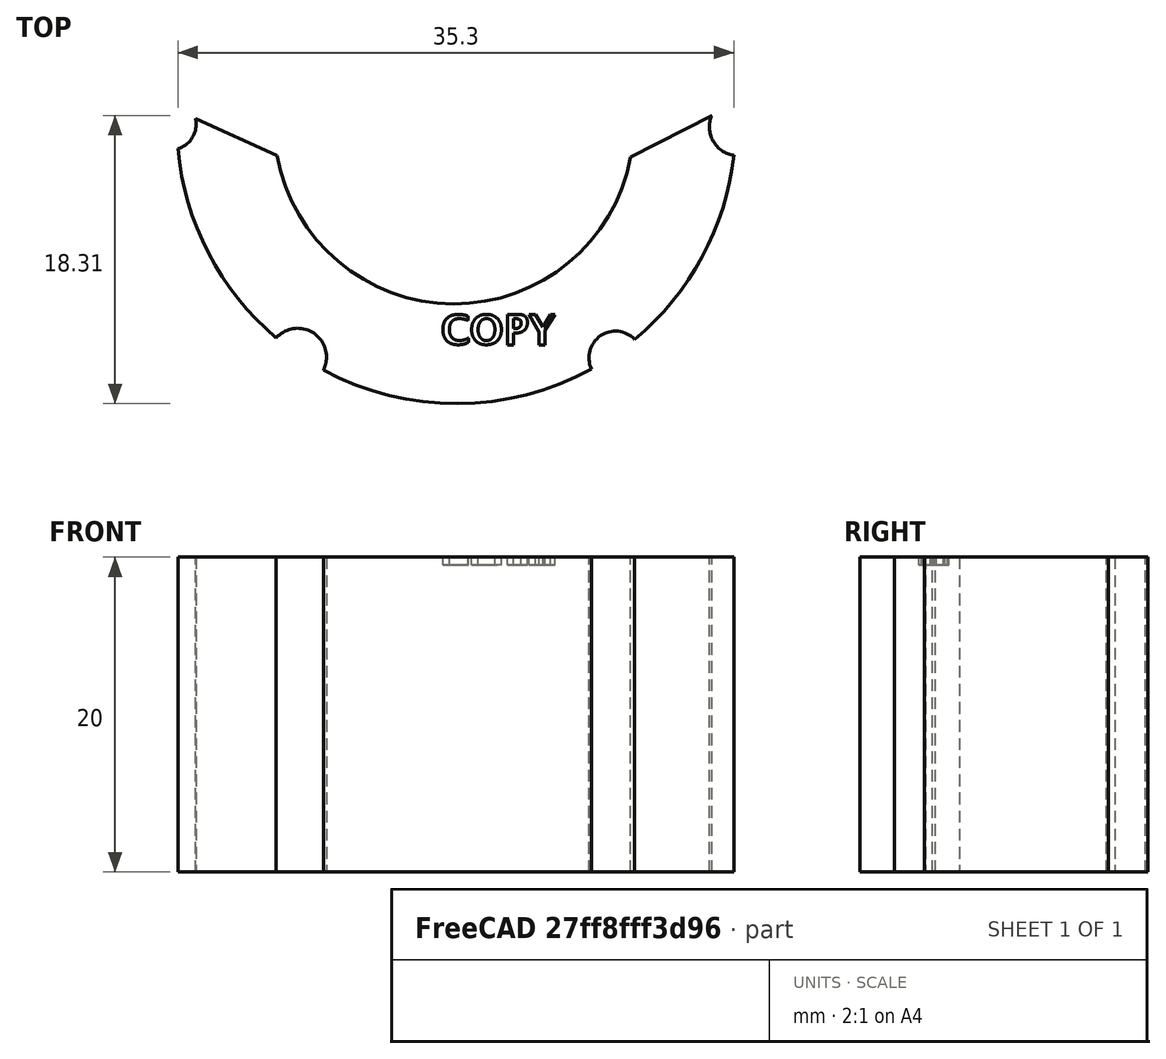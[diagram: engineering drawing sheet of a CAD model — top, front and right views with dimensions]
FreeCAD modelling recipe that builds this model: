
FCSTD DOCUMENT  (FreeCAD 0.18R4 (GitTag))
Label: Pad -copy
License: All rights reserved
LicenseURL: http://en.wikipedia.org/wiki/All_rights_reserved
objects: Sketcher::SketchObject×3, PartDesign::Pocket×2, PartDesign::Pad×1, PartDesign::Body×1, Part::Part2DObjectPython×1, Part::Extrusion×1, Part::Cut×1
note: 13 computed .brp shape members not serialized (recipe doc carries the construction recipe); baked Part::Feature solids carry a one-line shape summary decoded from their .brp

FEATURE [Sketcher::SketchObject] Sketch044
  MapMode = 5
  Support = -> [XY_Plane010]
  sketch-geometry (4):
    g0: ArcOfCircle CenterX=-0.026819 CenterY=0.000339 CenterZ=0 NormalX=0 NormalY=0 NormalZ=1 AngleXU=0 Radius=17.7391 StartAngle=3.09077 EndAngle=6.35772
    g1: ArcOfCircle CenterX=-0.16597 CenterY=0.00513446 CenterZ=0 NormalX=0 NormalY=0 NormalZ=1 AngleXU=0 Radius=11.4055 StartAngle=3.31589 EndAngle=6.09959
    g2: LineSegment StartX=-11.3987 StartY=-1.97276 StartZ=0 EndX=-17.743 EndY=0.901444 EndZ=0
    g3: LineSegment StartX=17.663 StartY=1.32135 StartZ=0 EndX=11.0479 EndY=-2.07709 EndZ=0
  constraints (4):
    c: Coincident(g2,g1)
    c: Coincident(g2,g0)
    c: Coincident(g3,g0)
    c: Coincident(g3,g1)
FEATURE [PartDesign::Pad] Pad013  label="Main body"
  Length = 20
  Length2 = 100
  Profile = -> Sketch044
  Type = 0
FEATURE [Sketcher::SketchObject] Sketch043
  MapMode = 5
  Placement = pos=(0,0,20) rot=(0,0,1;0rad)
  Support = -> [Pad013]
  sketch-geometry (2):
    g0: Circle CenterX=-18.1521 CenterY=0 CenterZ=0 NormalX=0 NormalY=0 NormalZ=1 AngleXU=0 Radius=1.5989
    g1: Circle CenterX=17.8665 CenterY=-0.158185 CenterZ=0 NormalX=0 NormalY=0 NormalZ=1 AngleXU=0 Radius=1.8237
  constraints (1):
    c: PointOnObject(g0,g-1)
FEATURE [PartDesign::Pocket] Pocket013  label="Edge guides"
  BaseFeature = -> Pad013
  Length = 5
  Length2 = 100
  Profile = -> Sketch043
  Type = 1
FEATURE [Sketcher::SketchObject] Sketch042
  MapMode = 5
  Placement = pos=(0,0,20) rot=(0,0,1;0rad)
  Support = -> [Pocket013]
  sketch-geometry (2):
    g0: Circle CenterX=-10.1009 CenterY=-14.7765 CenterZ=0 NormalX=0 NormalY=0 NormalZ=1 AngleXU=0 Radius=1.82777
    g1: Circle CenterX=10.0782 CenterY=-14.8185 CenterZ=0 NormalX=0 NormalY=0 NormalZ=1 AngleXU=0 Radius=1.68702
FEATURE [PartDesign::Pocket] Pocket014  label="Centre guides"
  BaseFeature = -> Pocket013
  Length = 5
  Length2 = 100
  Profile = -> Sketch042
  Type = 1
FEATURE [PartDesign::Body] Body010  label="Vial pad 22mm"
  Group = -> [Sketch044,Pad013,Sketch043,Pocket013,Sketch042,Pocket014]
  Origin = -> Origin010
  Placement = pos=(-50,0,40) rot=(0,0,1;0rad)
  Tip = -> Pocket014
FEATURE [Part::Part2DObjectPython] ShapeString001  label="Part number"  # Draft 2D object (typed FeaturePython)
  FontFile = C:/Program Files (x86)/Arduino/java/lib/fonts/LucidaSansDemiBold.ttf
  Size = 2
  String = COPY
  Tracking = 0
FEATURE [Part::Extrusion] Extrude
  Base = -> ShapeString001
  Dir = (0,0,1)
  DirMode = 2
  FaceMakerClass = Part::FaceMakerBullseye
  LengthFwd = 0.75
  LengthRev = 0
  Placement = pos=(-51,-14,59.5) rot=(0,0,1;0rad)
  Solid = false
  Symmetric = false
FEATURE [Part::Cut] Cut
  Base = -> Body010
  Tool = -> Extrude
